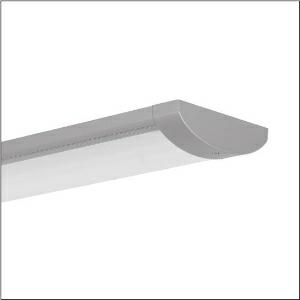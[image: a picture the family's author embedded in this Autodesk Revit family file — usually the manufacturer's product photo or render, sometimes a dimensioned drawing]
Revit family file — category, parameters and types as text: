
# Revit family: tv_20_5xa861d4n0j
name_source: partatom
category: Lighting Fixtures
units: mm (PartAtom-declared; Revit-internal decimal feet)

## family parameters
Cut with Voids When Loaded = No
Host = Face
Light Source = No
Part Type = Normal
Room Calculation Point = No
Round Connector Dimension = Use Diameter
Shared = No

## types (1)
- TV 20 (1 x LED 4000K / CRI = 80 (unbekannt), 3960 lm, 4000K)
    Apparent Load = 37 VA
    CIE Flux Codes = 48 78 95 99 100
    Color Rendering = 80
    Color Temperature = 4000K
    Default Elevation = 1800 mm
    Description = TV 20, vandal-proof luminaire, primary light control with specular reflector, of aluminium, matt, primary optical cover: enclosure, of PC, frosted, light emission: direct distribution, primary light characteristic: symmetric, installation type: surface-mounted, LED, rated luminous flux: 3.960lm, luminous efficacy: 107lm/W, light colour: 840, colour temperature: 4000K, control gear: DALI, mains connection: 230V, AC, 50Hz, rated input power: 37W, luminaire housing, of aluminium, coated, SITECO metallic grey (DB 702S), with wall and ceiling fixing element, length: 1.261mm, width: 260mm, height: 70mm, mounting height: 2.5..4.0m, protection rating (complete): IP65, insulation class (complete): insulation class I (protective earthing), certification: CE, protection symbol: F, impact resistance: 2x IK10, standard: EN 60598, packaging unit: 1 piece
    Height = 70 mm
    Lamp = 1 x LED 4000K / CRI >= 80 (unbekannt)
    Lamp Light Flux = 3960 lm
    Lamp count = 1
    Length = 1261 mm
    Luminous efficacy = 107 lm/W
    Manufacturer = Siteco
    ModVariant = No
    Model = 5XA861D4N0J
    Mounting Place = Ceiling
    Mounting Type = Surface mounted
    Number of Poles = 1
    OnlyDefault = Yes
    Power Factor = 1
    Product Name = TV 20
    Product group = vandal-proof luminaire
    ProductGroupID = 310
    Protection Class = Protection class I
    Protection Degree = IP 65
    RLX_Detail_Level = 1
    RLX_Emergency_Light_Flux = 0 lm
    RLX_Emergency_Type = 0
    RLX_Emergency_Type_DB = No
    RlxData = <blob elided: 25733 chars, md5=19f27cf6>
    Socket = socket
    Standby Power = 0 W
    System Light Flux = 3960 lm
    System Power = 37 W
    Type Comments = Product without accessories
    Type Image = l_1004809.jpg
    URL = http://relux.com
    VarID = ---
    Voltage = 0 V
    Weight = 0.00 kg
    Width = 260 mm

## geometry (parser evidence)
native form markers: Blend x4, Sweep x11
no freeform markers — native parametric forms only
